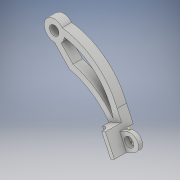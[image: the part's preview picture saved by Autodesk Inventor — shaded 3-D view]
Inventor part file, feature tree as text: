
AUTODESK INVENTOR PART (.ipt)
format: ipt  version: 2018 (Build 220112000, 112)  size: 215,552 bytes
history: native  units: in
note: dims shown in document units (in); Inventor stores cm internally (conversion verified against a paired STEP export)
features: sketch x11, extrude x7, plane x1, fillet x1
ambient origin geometry x8: Origin, YZ Plane, XZ Plane, XY Plane, X Axis, Y Axis, Z Axis, Center Point
bodies: Solid1 (feature_tree)
feature tree (20):
  sketch  "Sketch1"  dims[d15=1.0in d47=0.1969in d48=0.1969in]
  extrude  "Extrusion12"  Depth=0.1969in
  sketch  "Sketch16"  dims[d63=2.1654in d64=0.1969in]
  extrude  "Extrusion16"  Depth=0.1969in
  extrude  "Extrusion19"  Depth=0.7874in
  plane  "Work Plane9"
  sketch  "Sketch25"  dims[d75=0.2756in d76=0.2756in d77=0.0in]
  sketch  "Sketch26"  dims[d101=0.1181in d102=0.3937in d103=0.0in d106=0.5906in]
  extrude  "Extrusion20"  Depth=0.1969in
  sketch  "Sketch30"  dims[d118=0.4724in]
  extrude  "Extrusion21"  Depth=0.2756in TaperAngle=0.0deg
  extrude  "Extrusion22"  Depth=0.3937in TaperAngle=0.0deg
  fillet  "Fillet5"  Radius=0.5906in
  extrude  "Extrusion23"  Depth=0.1575in TaperAngle=0.0deg
  sketch  "Sketch19"  dims[d65=0.1969in d66=0.7874in]
  sketch  "Sketch24"  dims[d68=0.1969in d74=0.1969in]
  sketch  "Sketch27"  dims[d115=0.5906in d116=0.1575in d117=0.0in]
  sketch  "Sketch31"  dims[d119=0.1181in]
  sketch  "Sketch32"  dims[d120=0.374in]
  sketch  "Sketch33"  dims[d121=0.2165in d122=0.2362in d123=0.4724in d124=0.0in d129=0.2362in d130=0.1181in d131=0.2362in d132=0.1181in d133=0.4724in d134=0.0in d135=0.1516in d136=0.0in d139=0.1969in d140=0.2756in d141=0.1181in d142=0.0in d143=0.2362in d144=0.3937in d145=0.0in]
